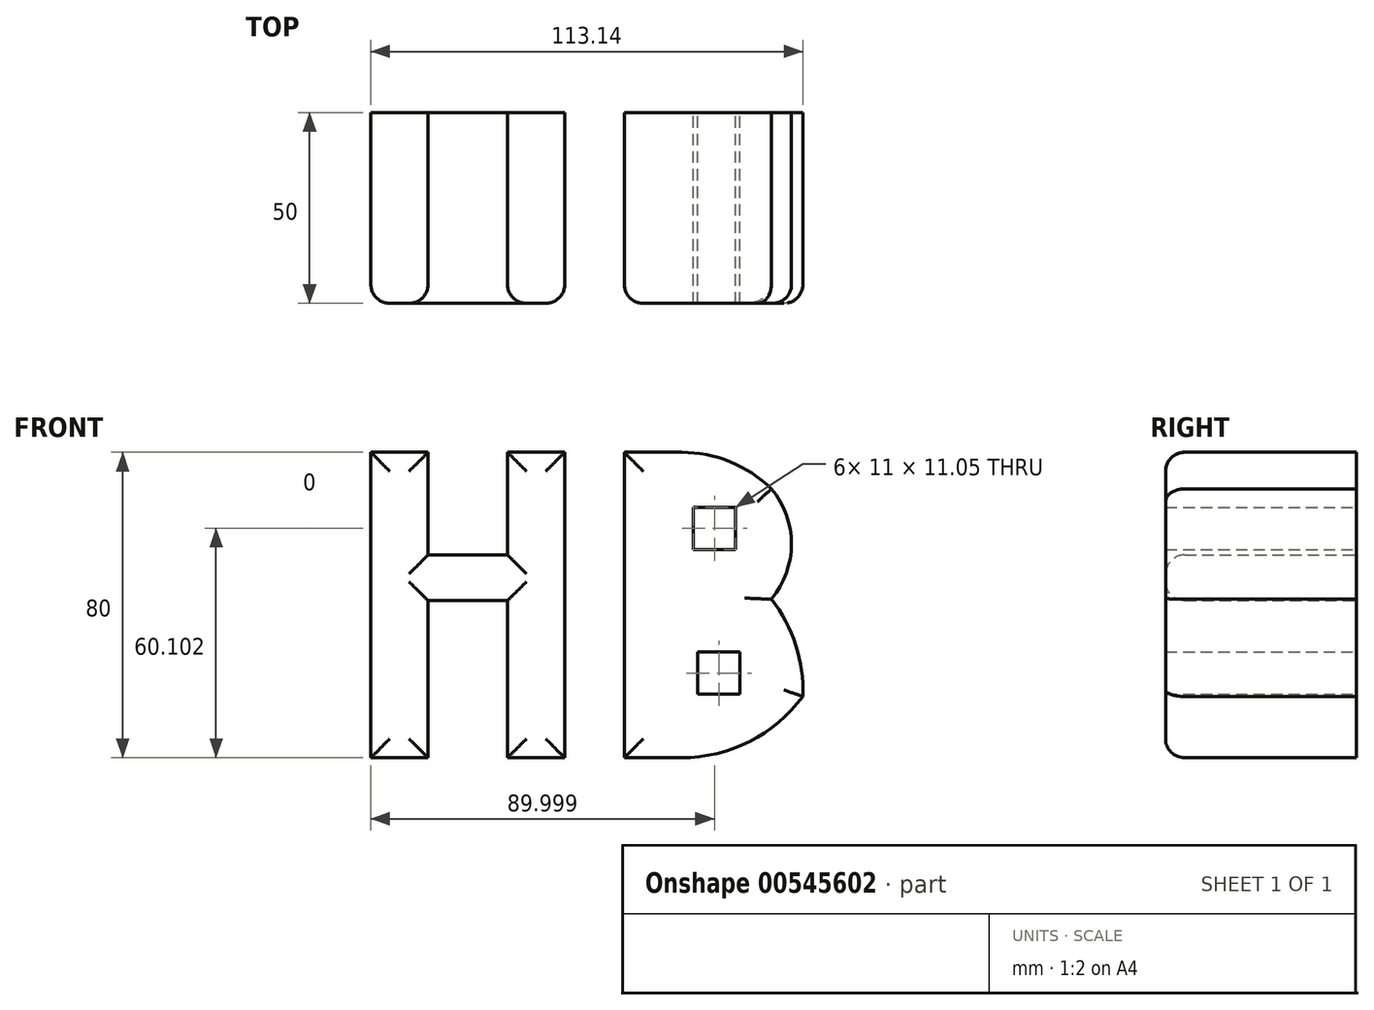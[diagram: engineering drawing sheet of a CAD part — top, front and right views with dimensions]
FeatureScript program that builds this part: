
annotation { "Feature Type Name" : "Feature", "Feature Type Description" : "" }
export const myFeature = defineFeature(function(context is Context, id is Id, definition is map)
    precondition{}
    {
        {
            var Q0;
            Q0=qCreatedBy(makeId("Front.planeOp"),FACE);
            var sketch = newSketch(context, id + "F0", { "sketchPlane" : qUnion([Q0])});
            skLineSegment(sketch, "E0.bottom", {"start": v(-50.79, 33.07) * mm, "end": v(-35.79, 33.07) * mm});
            skLineSegment(sketch, "E0.top", {"start": v(-50.79, -46.93) * mm, "end": v(-35.79, -46.93) * mm});
            skLineSegment(sketch, "E0.left", {"start": v(-50.79, 33.07) * mm, "end": v(-50.79, -46.93) * mm});
            skLineSegment(sketch, "E0.right", {"start": v(-35.79, 33.07) * mm, "end": v(-35.79, 6.21) * mm});
            skLineSegment(sketch, "E1.bottom", {"start": v(-35.79, 6.21) * mm, "end": v(-15, 6.21) * mm});
            skLineSegment(sketch, "E1.top", {"start": v(-35.79, -5.79) * mm, "end": v(-15, -5.79) * mm});
            skLineSegment(sketch, "E2.bottom", {"start": v(-15, 33.07) * mm, "end": v(0, 33.07) * mm});
            skLineSegment(sketch, "E2.top", {"start": v(-15, -46.93) * mm, "end": v(0, -46.93) * mm});
            skLineSegment(sketch, "E2.left", {"start": v(-15, 33.07) * mm, "end": v(-15, 6.21) * mm});
            skLineSegment(sketch, "E2.right", {"start": v(0, 33.07) * mm, "end": v(0, -46.93) * mm});
            skLineSegment(sketch, "E3.trimOffspring", {"start": v(-15, -5.79) * mm, "end": v(-15, -46.93) * mm});
            skLineSegment(sketch, "E4.trimOffspring", {"start": v(-35.79, -5.79) * mm, "end": v(-35.79, -46.93) * mm});
            skPoint(sketch, "E5.firstSnap0", {"position": v(-7.5, 33.07) * mm});
            skLineSegment(sketch, "E5.bottom", {"start": v(15.58, 33.07) * mm, "end": v(30.58, 33.07) * mm});
            skLineSegment(sketch, "E5.top", {"start": v(15.58, -46.93) * mm, "end": v(30.58, -46.93) * mm});
            skLineSegment(sketch, "E5.left", {"start": v(15.58, 33.07) * mm, "end": v(15.58, -46.93) * mm});
            skArc(sketch, "E6", {"start": v(54.1, 23.51) * mm, "mid": v(43.28, 30.6) * mm, "end": v(30.58, 33.07) * mm});
            skArc(sketch, "E7", {"start": v(54.1, -5.38) * mm, "mid": v(59.35, 9.06) * mm, "end": v(54.1, 23.51) * mm});
            skArc(sketch, "E8", {"start": v(62.32, -30.88) * mm, "mid": v(60.45, -17.4) * mm, "end": v(54.1, -5.38) * mm});
            skArc(sketch, "E9", {"start": v(30.58, -46.93) * mm, "mid": v(48.36, -42.69) * mm, "end": v(62.32, -30.88) * mm});
            skLineSegment(sketch, "E10.bottom", {"start": v(33.7, 18.7) * mm, "end": v(44.7, 18.7) * mm});
            skLineSegment(sketch, "E10.top", {"start": v(33.7, 7.65) * mm, "end": v(44.7, 7.65) * mm});
            skLineSegment(sketch, "E10.left", {"start": v(33.7, 18.7) * mm, "end": v(33.7, 7.65) * mm});
            skLineSegment(sketch, "E10.right", {"start": v(44.7, 18.7) * mm, "end": v(44.7, 7.65) * mm});
            skLineSegment(sketch, "E11.bottom", {"start": v(34.84, -19.26) * mm, "end": v(45.84, -19.26) * mm});
            skLineSegment(sketch, "E11.top", {"start": v(34.84, -30.31) * mm, "end": v(45.84, -30.31) * mm});
            skLineSegment(sketch, "E11.left", {"start": v(34.84, -19.26) * mm, "end": v(34.84, -30.31) * mm});
            skLineSegment(sketch, "E11.right", {"start": v(45.84, -19.26) * mm, "end": v(45.84, -30.31) * mm});
            skSolve(sketch);
        }
        {
            var Q0;
            Q0 = qSketchRegion(id + "F0", true);
            extrude(context, id + "F1", {"entities" : qUnion([Q0]), "depth" : 50 * mm, "offsetDistance" : 25 * mm});
        }
        {
            var Q0;
            Q0=makeQuery(id+"F1.opExtrude","CAP_EDGE",EDGE,{"disambiguationData":[OSD([sQuery(id+"F0.wireOp",EDGE,"E6")])],"isStart":false});
            var Q1;
            Q1=makeQuery(id+"F1.opExtrude","CAP_EDGE",EDGE,{"disambiguationData":[OSD([sQuery(id+"F0.wireOp",EDGE,"E7")])],"isStart":false});
            var Q2;
            Q2=makeQuery(id+"F1.opExtrude","CAP_EDGE",EDGE,{"disambiguationData":[OSD([sQuery(id+"F0.wireOp",EDGE,"E8")])],"isStart":false});
            var Q3;
            Q3=makeQuery(id+"F1.opExtrude","CAP_EDGE",EDGE,{"disambiguationData":[OSD([sQuery(id+"F0.wireOp",EDGE,"E9")])],"isStart":false});
            var Q4;
            Q4=makeQuery(id+"F1.opExtrude","CAP_EDGE",EDGE,{"disambiguationData":[OSD([sQuery(id+"F0.wireOp",EDGE,"E5.top")])],"isStart":false});
            var Q5;
            Q5=makeQuery(id+"F1.opExtrude","CAP_EDGE",EDGE,{"disambiguationData":[OSD([sQuery(id+"F0.wireOp",EDGE,"E5.left")])],"isStart":false});
            var Q6;
            Q6=makeQuery(id+"F1.opExtrude","CAP_EDGE",EDGE,{"disambiguationData":[OSD([sQuery(id+"F0.wireOp",EDGE,"E2.right")])],"isStart":false});
            var Q7;
            Q7=makeQuery(id+"F1.opExtrude","CAP_EDGE",EDGE,{"disambiguationData":[OSD([sQuery(id+"F0.wireOp",EDGE,"E2.bottom")])],"isStart":false});
            var Q8;
            Q8=makeQuery(id+"F1.opExtrude","CAP_FACE",FACE,{"disambiguationData":[OSD([sQuery(id+"F0.wireOp",EDGE,"E0.bottom"),sQuery(id+"F0.wireOp",EDGE,"E0.top"),sQuery(id+"F0.wireOp",EDGE,"E0.left"),sQuery(id+"F0.wireOp",EDGE,"E0.right"),sQuery(id+"F0.wireOp",EDGE,"E1.bottom"),sQuery(id+"F0.wireOp",EDGE,"E1.top"),sQuery(id+"F0.wireOp",EDGE,"E2.bottom"),sQuery(id+"F0.wireOp",EDGE,"E2.top"),sQuery(id+"F0.wireOp",EDGE,"E2.left"),sQuery(id+"F0.wireOp",EDGE,"E2.right"),sQuery(id+"F0.wireOp",EDGE,"E3.trimOffspring"),sQuery(id+"F0.wireOp",EDGE,"E4.trimOffspring")])],"isStart":false});
            fillet(context, id + "F2", {"entities" : qUnion([Q0, Q1, Q2, Q3, Q4, Q5, Q6, Q7, Q8]), "radius" : 5 * mm, "tangentPropagation" : true, "allowEdgeOverflow" : false});
        }
    });
